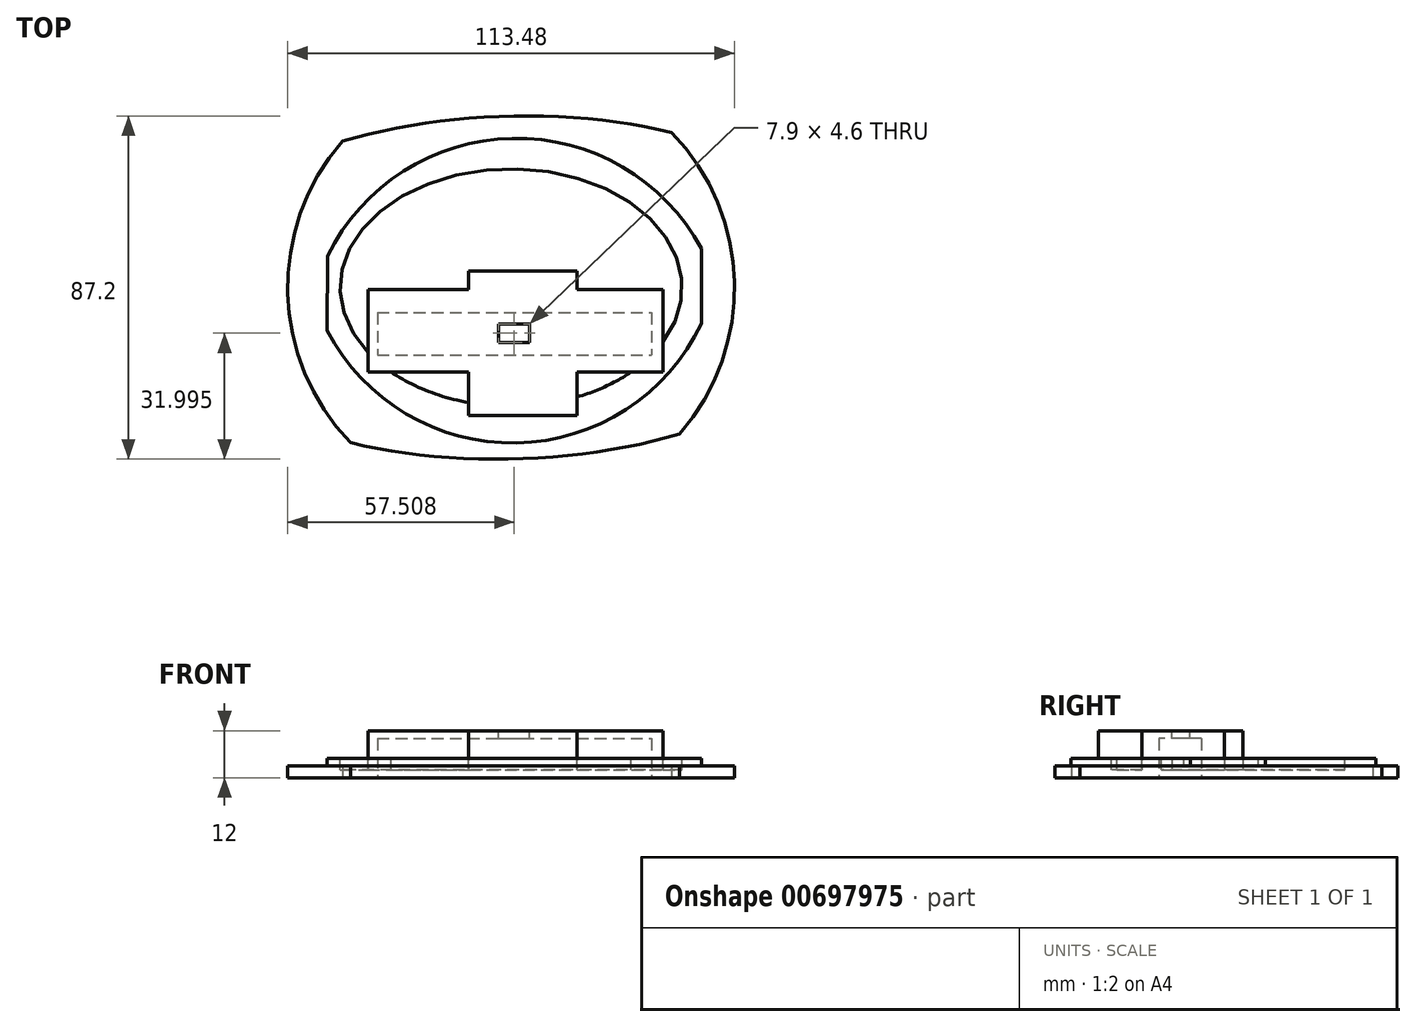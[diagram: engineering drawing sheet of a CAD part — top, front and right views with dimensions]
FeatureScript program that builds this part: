
annotation { "Feature Type Name" : "Feature", "Feature Type Description" : "" }
export const myFeature = defineFeature(function(context is Context, id is Id, definition is map)
    precondition{}
    {
        {
            var Q0;
            Q0=qCreatedBy(makeId("Top.planeOp"),FACE);
            var sketch = newSketch(context, id + "F0", { "sketchPlane" : qUnion([Q0])});
            skLineSegment(sketch, "E0.left", {"start": v(-46.64, 8.05) * mm, "end": v(-46.69, -10.95) * mm});
            skLineSegment(sketch, "E0.right", {"start": v(48.37, 9.9) * mm, "end": v(48.32, -9.1) * mm});
            skPoint(sketch, "E1.endSnap0", {"position": v(0, -24.76) * mm});
            skArc(sketch, "E2", {"start": v(48.37, 9.9) * mm, "mid": v(0.3, 37.9) * mm, "end": v(-46.64, 8.05) * mm});
            skArc(sketch, "E3", {"start": v(-46.69, -10.95) * mm, "mid": v(1.4, -39.5) * mm, "end": v(48.32, -9.1) * mm});
            skPoint(sketch, "E1.end.orphan", {"position": v(0, -39.5) * mm});
            skEllipticalArc(sketch, "E4", {});
            skEllipticalArc(sketch, "E5.trimOffspring", {});
            skPoint(sketch, "E6.start.orphan", {"position": v(0.3, 37.9) * mm});
            skArc(sketch, "E7", {"start": v(42.85, -37.2) * mm, "mid": v(56.72, 1.52) * mm, "end": v(40.8, 39.43) * mm});
            skArc(sketch, "E8.trimOffspring", {"start": v(-42.85, 37.2) * mm, "mid": v(-56.72, -1.52) * mm, "end": v(-40.8, -39.43) * mm});
            const initialGuessF0  = {"E4": [0, 0, 0.9996431337373777, 0.02671338937153828, 0.0880768689629508, 0.04355424366850744, 4.217423522181871, 5.207354438587494], "E5.trimOffspring": [0, 0, 0.9996431337373777, 0.02671338937153828, 0.0880768689629508, 0.04355424366850744, 1.0758308685920797, 2.065761784997701]};
            skSetInitialGuess(sketch, initialGuessF0);
            skSolve(sketch);
        }
        {
            var Q0;
            Q0=makeQuery(id+"F0.imprint","IMPRINT",FACE,{"disambiguationData":[TD([[makeQuery(id+"F0.imprint","IMPRINT",EDGE,{"derivedFrom":sQuery(id+"F0.wireOp",EDGE,"E0.left")}),-1.0]])]});
            extrude(context, id + "F1", {"entities" : qUnion([Q0]), "depth" : 3 * mm, "offsetDistance" : 25 * mm});
        }
        {
            var Q0;
            Q0=makeQuery(id+"F0.imprint","IMPRINT",FACE,{"disambiguationData":[TD([[makeQuery(id+"F0.imprint","IMPRINT",EDGE,{"derivedFrom":sQuery(id+"F0.wireOp",EDGE,"E0.left")}),1.0]])]});
            extrude(context, id + "F2", {"entities" : qUnion([Q0]), "operationType" : NewBodyOperationType.ADD, "depth" : 5 * mm, "offsetDistance" : 25 * mm});
        }
        {
            var Q0;
            Q0=makeQuery(id+"F2.opExtrude","CAP_FACE",FACE,{"disambiguationData":[OSD([sQuery(id+"F0.wireOp",EDGE,"E0.left"),sQuery(id+"F0.wireOp",EDGE,"E0.right"),sQuery(id+"F0.wireOp",EDGE,"E2"),sQuery(id+"F0.wireOp",EDGE,"E3")])],"isStart":false});
            var sketch = newSketch(context, id + "F3", { "sketchPlane" : qUnion([Q0])});
            skEllipse(sketch, "E9", {"center": v(0, 0) * mm, "majorRadius": 43.4 * mm, "minorRadius": 30.15 * mm, "majorAxis": v(-1, 0)});
            skSolve(sketch);
        }
        {
            var Q0;
            Q0 = qSketchRegion(id + "F3", true);
            extrude(context, id + "F4", {"entities" : qUnion([Q0]), "operationType" : NewBodyOperationType.REMOVE, "oppositeDirection" : true, "depth" : 3 * mm, "offsetDistance" : 25 * mm});
        }
        {
            var Q0;
            Q0=makeQuery(id+"F4.boolean.opBoolean","COPY",FACE,{"derivedFrom":makeQuery(id+"F4.opExtrude","CAP_FACE",FACE,{"disambiguationData":[OSD([sQuery(id+"F3.wireOp",EDGE,"E9")])],"isStart":false})});
            var sketch = newSketch(context, id + "F5", { "sketchPlane" : qUnion([Q0])});
            skLineSegment(sketch, "E10.bottom", {"start": v(-36.35, -21.44) * mm, "end": v(-10.79, -21.44) * mm});
            skLineSegment(sketch, "E10.top", {"start": v(-36.35, -0.53) * mm, "end": v(-10.79, -0.53) * mm});
            skLineSegment(sketch, "E10.left", {"start": v(-36.35, -21.44) * mm, "end": v(-36.35, -0.53) * mm});
            skLineSegment(sketch, "E10.right", {"start": v(38.65, -21.44) * mm, "end": v(38.65, -0.53) * mm});
            skLineSegment(sketch, "E11.bottom", {"start": v(-10.79, 4.21) * mm, "end": v(16.78, 4.21) * mm});
            skLineSegment(sketch, "E11.top", {"start": v(-10.79, -32.55) * mm, "end": v(16.78, -32.55) * mm});
            skLineSegment(sketch, "E11.left", {"start": v(-10.79, 4.21) * mm, "end": v(-10.79, -0.53) * mm});
            skLineSegment(sketch, "E11.right", {"start": v(16.78, 4.21) * mm, "end": v(16.78, -0.53) * mm});
            skLineSegment(sketch, "E12.trimOffspring", {"start": v(16.78, -0.53) * mm, "end": v(38.65, -0.53) * mm});
            skLineSegment(sketch, "E13.trimOffspring", {"start": v(16.78, -21.44) * mm, "end": v(38.65, -21.44) * mm});
            skLineSegment(sketch, "E14.trimOffspring", {"start": v(-10.79, -21.44) * mm, "end": v(-10.79, -32.55) * mm});
            skLineSegment(sketch, "E15.trimOffspring", {"start": v(16.78, -21.44) * mm, "end": v(16.78, -32.55) * mm});
            skSolve(sketch);
        }
        {
            var Q0;
            Q0 = qSketchRegion(id + "F5", true);
            extrude(context, id + "F6", {"entities" : qUnion([Q0]), "operationType" : NewBodyOperationType.ADD, "depth" : 10 * mm, "offsetDistance" : 25 * mm});
        }
        {
            var Q0;
            Q0=makeQuery(id+"F6.opExtrude","CAP_FACE",FACE,{"disambiguationData":[OSD([sQuery(id+"F5.wireOp",EDGE,"E10.bottom"),sQuery(id+"F5.wireOp",EDGE,"E10.top"),sQuery(id+"F5.wireOp",EDGE,"E10.left"),sQuery(id+"F5.wireOp",EDGE,"E10.right")])],"isStart":false});
            var sketch = newSketch(context, id + "F7", { "sketchPlane" : qUnion([Q0])});
            skLineSegment(sketch, "E16.bottom", {"start": v(-33.94, -6.4) * mm, "end": v(35.74, -6.4) * mm});
            skLineSegment(sketch, "E16.top", {"start": v(-33.94, -17.16) * mm, "end": v(35.74, -17.16) * mm});
            skLineSegment(sketch, "E16.left", {"start": v(-33.94, -6.4) * mm, "end": v(-33.94, -17.16) * mm});
            skLineSegment(sketch, "E16.right", {"start": v(35.74, -6.4) * mm, "end": v(35.74, -17.16) * mm});
            skSolve(sketch);
        }
        {
            var Q0;
            Q0 = qSketchRegion(id + "F7", true);
            extrude(context, id + "F8", {"entities" : qUnion([Q0]), "operationType" : NewBodyOperationType.ADD, "oppositeDirection" : true, "depth" : 25 * mm, "offsetDistance" : 25 * mm});
        }
        {
            var Q0;
            Q0=makeQuery(id+"F8.opExtrude","CAP_FACE",FACE,{"disambiguationData":[OSD([sQuery(id+"F7.wireOp",EDGE,"E16.bottom"),sQuery(id+"F7.wireOp",EDGE,"E16.top"),sQuery(id+"F7.wireOp",EDGE,"E16.left"),sQuery(id+"F7.wireOp",EDGE,"E16.right")])],"isStart":false});
            extrude(context, id + "F9", {"entities" : qUnion([Q0]), "operationType" : NewBodyOperationType.REMOVE, "oppositeDirection" : true, "depth" : 23 * mm, "offsetDistance" : 25 * mm});
        }
        {
            var Q0;
            Q0=makeQuery(id+"F6.opExtrude","CAP_FACE",FACE,{"disambiguationData":[OSD([sQuery(id+"F5.wireOp",EDGE,"E10.bottom"),sQuery(id+"F5.wireOp",EDGE,"E10.top"),sQuery(id+"F5.wireOp",EDGE,"E10.left"),sQuery(id+"F5.wireOp",EDGE,"E10.right"),sQuery(id+"F5.wireOp",EDGE,"E11.bottom"),sQuery(id+"F5.wireOp",EDGE,"E11.top"),sQuery(id+"F5.wireOp",EDGE,"E11.left"),sQuery(id+"F5.wireOp",EDGE,"E11.right"),sQuery(id+"F5.wireOp",EDGE,"E12.trimOffspring"),sQuery(id+"F5.wireOp",EDGE,"E13.trimOffspring"),sQuery(id+"F5.wireOp",EDGE,"E14.trimOffspring"),sQuery(id+"F5.wireOp",EDGE,"E15.trimOffspring")])],"isStart":false});
            var sketch = newSketch(context, id + "F10", { "sketchPlane" : qUnion([Q0])});
            skLineSegment(sketch, "E17.bottom", {"start": v(-3.18, -9.3) * mm, "end": v(4.72, -9.3) * mm});
            skLineSegment(sketch, "E17.top", {"start": v(-3.18, -13.9) * mm, "end": v(4.72, -13.9) * mm});
            skLineSegment(sketch, "E17.left", {"start": v(-3.18, -9.3) * mm, "end": v(-3.18, -13.9) * mm});
            skLineSegment(sketch, "E17.right", {"start": v(4.72, -9.3) * mm, "end": v(4.72, -13.9) * mm});
            skSolve(sketch);
        }
        {
            var Q0;
            Q0 = qSketchRegion(id + "F10", true);
            extrude(context, id + "F11", {"entities" : qUnion([Q0]), "operationType" : NewBodyOperationType.REMOVE, "oppositeDirection" : true, "depth" : 25 * mm, "offsetDistance" : 25 * mm});
        }
    });
